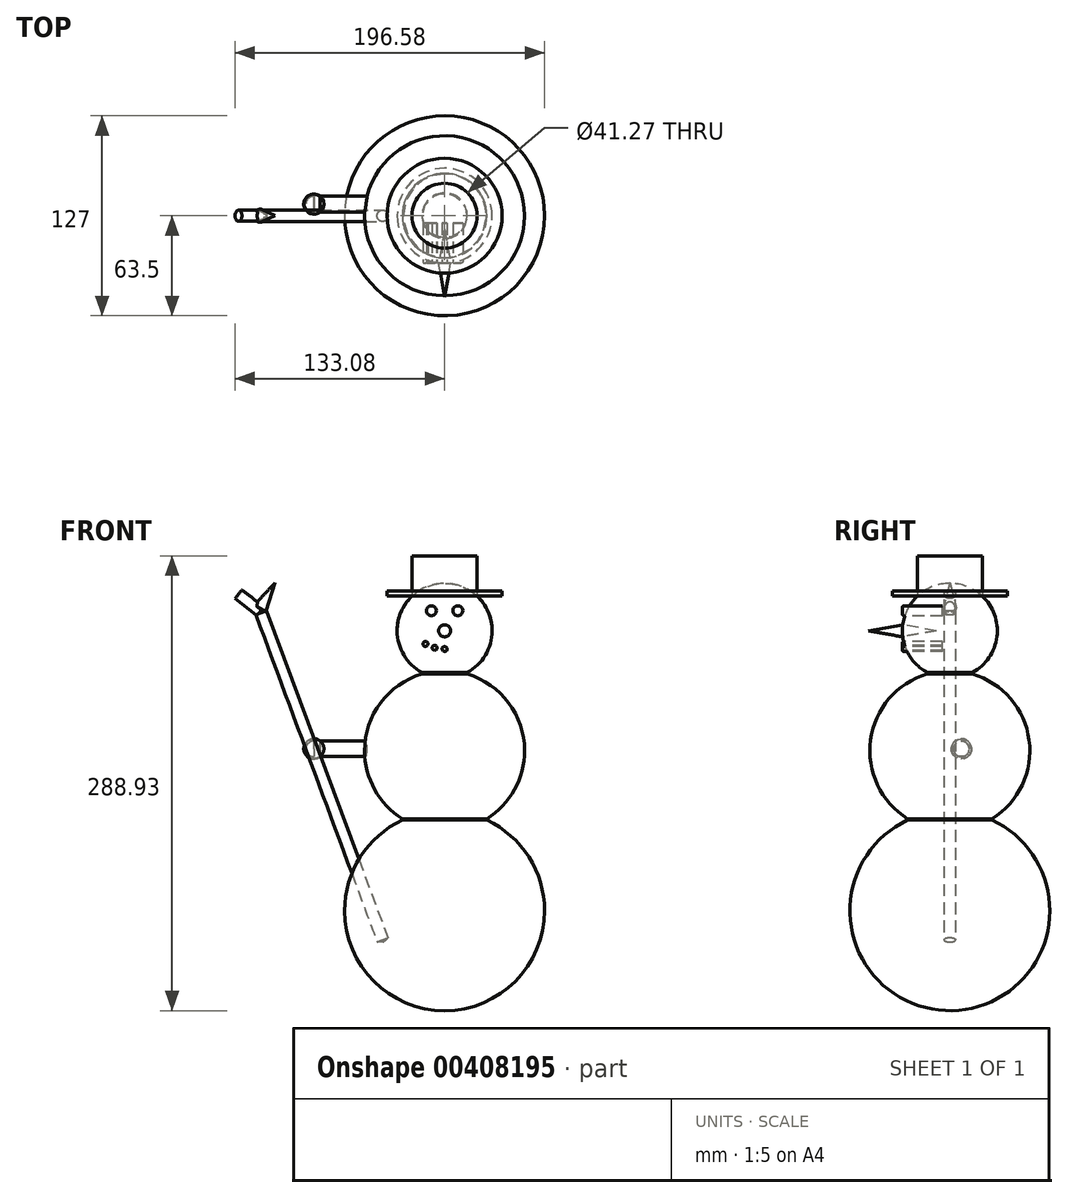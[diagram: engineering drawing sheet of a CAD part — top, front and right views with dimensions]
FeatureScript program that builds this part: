
annotation { "Feature Type Name" : "Feature", "Feature Type Description" : "" }
export const myFeature = defineFeature(function(context is Context, id is Id, definition is map)
    precondition{}
    {
        {
            var Q0;
            Q0=qCreatedBy(makeId("Top.planeOp"),FACE);
            var sketch = newSketch(context, id + "F0", { "sketchPlane" : qUnion([Q0])});
            skArc(sketch, "E0", {"start": v(63.5, 0) * mm, "mid": v(0, 63.5) * mm, "end": v(-63.5, 0) * mm});
            skLineSegment(sketch, "E1", {"start": v(-63.5, 0) * mm, "end": v(63.5, 0) * mm});
            skSolve(sketch);
        }
        {
            var Q0;
            Q0=qSketchRegion(id+"F0",true);
            var Q1;
            Q1=sQuery(id+"F0.wireOp",EDGE,"E1");
            revolve(context, id + "F1", {"entities" : qUnion([Q0]), "axis" : qUnion([Q1]), "revolveType" : RevolveType.FULL});
        }
        {
            var Q0;
            Q0=qCreatedBy(makeId("Front.planeOp"),FACE);
            var sketch = newSketch(context, id + "F2", { "sketchPlane" : qUnion([Q0])});
            skLineSegment(sketch, "E2", {"start": v(0, 0) * mm, "end": v(0, 50.8) * mm});
            skArc(sketch, "E3", {"start": v(-50.8, 101.6) * mm, "mid": v(0, 50.8) * mm, "end": v(50.8, 101.6) * mm});
            skLineSegment(sketch, "E4", {"start": v(0, 101.6) * mm, "end": v(50.8, 101.6) * mm});
            skLineSegment(sketch, "E5", {"start": v(50.8, 101.6) * mm, "end": v(0, 101.6) * mm});
            skLineSegment(sketch, "E6", {"start": v(-50.8, 101.6) * mm, "end": v(0, 101.6) * mm});
            skSolve(sketch);
        }
        {
            var Q0;
            Q0=qSketchRegion(id+"F2",true);
            var Q1;
            Q1=sQuery(id+"F2.wireOp",EDGE,"E5");
            revolve(context, id + "F3", {"operationType" : NewBodyOperationType.ADD, "entities" : qUnion([Q0]), "axis" : qUnion([Q1]), "revolveType" : RevolveType.FULL});
        }
        {
            var Q0;
            Q0=qCreatedBy(makeId("Front.planeOp"),FACE);
            var sketch = newSketch(context, id + "F4", { "sketchPlane" : qUnion([Q0])});
            skLineSegment(sketch, "E7", {"start": v(0, 177.8) * mm, "end": v(0, 0) * mm});
            skArc(sketch, "E8", {"start": v(30.16, 177.8) * mm, "mid": v(0, 207.96) * mm, "end": v(-30.16, 177.8) * mm});
            skLineSegment(sketch, "E9", {"start": v(0, 177.8) * mm, "end": v(30.16, 177.8) * mm});
            skLineSegment(sketch, "E10", {"start": v(0, 177.8) * mm, "end": v(-30.16, 177.8) * mm});
            skSolve(sketch);
        }
        {
            var Q0;
            Q0=qSketchRegion(id+"F4",true);
            var Q1;
            Q1=sQuery(id+"F4.wireOp",EDGE,"E10");
            revolve(context, id + "F5", {"operationType" : NewBodyOperationType.ADD, "entities" : qUnion([Q0]), "axis" : qUnion([Q1]), "revolveType" : RevolveType.FULL});
        }
        {
            var Q0;
            Q0=makeQuery(id+"F3.boolean.opBoolean","INTERSECT",EDGE,{"derivedFrom":[makeQuery(id+"F1.opRevolve","SWEPT_FACE",FACE,{"disambiguationData":[OSD([sQuery(id+"F0.wireOp",EDGE,"E0")])]}),makeQuery(id+"F3.opRevolve","SWEPT_FACE",FACE,{"disambiguationData":[OSD([sQuery(id+"F2.wireOp",EDGE,"E3")])]})]});
            var Q1;
            Q1=makeQuery(id+"F5.boolean.opBoolean","INTERSECT",EDGE,{"derivedFrom":[makeQuery(id+"F3.opRevolve","SWEPT_FACE",FACE,{"disambiguationData":[OSD([sQuery(id+"F2.wireOp",EDGE,"E3")])]}),makeQuery(id+"F5.opRevolve","SWEPT_FACE",FACE,{"disambiguationData":[OSD([sQuery(id+"F4.wireOp",EDGE,"E8")])]})]});
            fillet(context, id + "F6", {"entities" : qUnion([Q0, Q1]), "radius" : 0.5 * mm, "tangentPropagation" : true, "allowEdgeOverflow" : false});
        }
        {
            var Q0;
            Q0=qCreatedBy(makeId("Front.planeOp"),FACE);
            cPlane(context, id + "F7", {"entities" : qUnion([Q0]), "cplaneType" : CPlaneType.OFFSET, "offset" : 30.16 * mm, "width" : 152.4 * mm, "height" : 152.4 * mm});
        }
        {
            var Q0;
            Q0=qCreatedBy(id+"F7.planeOp",FACE);
            var sketch = newSketch(context, id + "F8", { "sketchPlane" : qUnion([Q0])});
            skLineSegment(sketch, "E11", {"start": v(0, 0) * mm, "end": v(0, 177.8) * mm});
            skCircle(sketch, "E12", {"center": v(-8.4, 190.52) * mm, "radius": 3.18 * mm});
            skCircle(sketch, "E13", {"center": v(8.4, 190.52) * mm, "radius": 3.18 * mm});
            skCircle(sketch, "E14", {"center": v(0, 177.8) * mm, "radius": 3.81 * mm});
            skCircle(sketch, "E15", {"center": v(0, 166.2) * mm, "radius": 1.59 * mm});
            skCircle(sketch, "E16.1.0", {"center": v(-6.3, 167.03) * mm, "radius": 1.59 * mm});
            skCircle(sketch, "E16.2.0", {"center": v(-12.16, 169.46) * mm, "radius": 1.59 * mm});
            skPoint(sketch, "E16.center", {"position": v(0, 190.52) * mm});
            skCircle(sketch, "E17.MirrorC", {"center": v(6.3, 167.03) * mm, "radius": 1.59 * mm});
            skCircle(sketch, "E18.MirrorC", {"center": v(12.16, 169.46) * mm, "radius": 1.59 * mm});
            skSolve(sketch);
        }
        {
            var Q0;
            Q0=makeQuery(id+"F8.imprint","IMPRINT",FACE,{"disambiguationData":[TD([[makeQuery(id+"F8.imprint","IMPRINT",EDGE,{"derivedFrom":sQuery(id+"F8.wireOp",EDGE,"E12")}),1.0]])]});
            var Q1;
            Q1=makeQuery(id+"F8.imprint","IMPRINT",FACE,{"disambiguationData":[TD([[makeQuery(id+"F8.imprint","IMPRINT",EDGE,{"derivedFrom":sQuery(id+"F8.wireOp",EDGE,"E13")}),1.0]])]});
            var Q2;
            Q2=makeQuery(id+"F8.imprint","IMPRINT",FACE,{"disambiguationData":[TD([[makeQuery(id+"F8.imprint","IMPRINT",EDGE,{"derivedFrom":sQuery(id+"F8.wireOp",EDGE,"E16.2.0")}),1.0]])]});
            var Q3;
            Q3=makeQuery(id+"F8.imprint","IMPRINT",FACE,{"disambiguationData":[TD([[makeQuery(id+"F8.imprint","IMPRINT",EDGE,{"derivedFrom":sQuery(id+"F8.wireOp",EDGE,"E16.1.0")}),1.0]])]});
            var Q4;
            {var subQ0=sQuery(id+"F8.wireOp",EDGE,"E15");var subQ1=sQuery(id+"F8.wireOp",EDGE,"E11");var subQ2=makeQuery(id+"F8.imprint","INTERSECT",VERTEX,{"disambiguationData":[OD(0.0)],"derivedFrom":[subQ1,subQ0]});Q4=makeQuery(id+"F8.imprint","IMPRINT",FACE,{"disambiguationData":[TD([[makeQuery(id+"F8.imprint","IMPRINT",EDGE,{"disambiguationData":[TD([[subQ2,-1.0]])],"derivedFrom":subQ1}),-1.0]])]});}
            var Q5;
            Q5=makeQuery(id+"F8.imprint","IMPRINT",FACE,{"disambiguationData":[TD([[makeQuery(id+"F8.imprint","IMPRINT",EDGE,{"derivedFrom":sQuery(id+"F8.wireOp",EDGE,"E17.MirrorC")}),-1.0]])]});
            var Q6;
            Q6=makeQuery(id+"F8.imprint","IMPRINT",FACE,{"disambiguationData":[TD([[makeQuery(id+"F8.imprint","IMPRINT",EDGE,{"derivedFrom":sQuery(id+"F8.wireOp",EDGE,"E18.MirrorC")}),-1.0]])]});
            var Q7;
            {var subQ0=sQuery(id+"F8.wireOp",EDGE,"E15");var subQ1=sQuery(id+"F8.wireOp",EDGE,"E11");var subQ2=makeQuery(id+"F8.imprint","INTERSECT",VERTEX,{"disambiguationData":[OD(0.0)],"derivedFrom":[subQ1,subQ0]});Q7=makeQuery(id+"F8.imprint","IMPRINT",FACE,{"disambiguationData":[TD([[makeQuery(id+"F8.imprint","IMPRINT",EDGE,{"disambiguationData":[TD([[subQ2,-1.0]])],"derivedFrom":subQ1}),1.0]])]});}
            var Q8;
            Q8=sQuery(id+"F8.wireOp",EDGE,"E12");
            var Q9;
            Q9=sQuery(id+"F8.wireOp",EDGE,"E13");
            var Q10;
            Q10=sQuery(id+"F8.wireOp",EDGE,"E18.MirrorC");
            var Q11;
            Q11=sQuery(id+"F8.wireOp",EDGE,"E17.MirrorC");
            var Q12;
            Q12=sQuery(id+"F8.wireOp",EDGE,"E15");
            var Q13;
            Q13=sQuery(id+"F8.wireOp",EDGE,"E16.1.0");
            var Q14;
            Q14=sQuery(id+"F8.wireOp",EDGE,"E16.2.0");
            extrude(context, id + "F9", {"entities" : qUnion([Q0, Q1, Q2, Q3, Q4, Q5, Q6, Q7]), "surfaceEntities" : qUnion([Q8, Q9, Q10, Q11, Q12, Q13, Q14]), "oppositeDirection" : true, "depth" : 25.4 * mm});
        }
        {
            var Q0;
            Q0=makeQuery(id+"F9.opExtrude","CAP_EDGE",EDGE,{"disambiguationData":[OSD([sQuery(id+"F8.wireOp",EDGE,"E12")])],"isStart":true});
            var Q1;
            Q1=makeQuery(id+"F9.opExtrude","CAP_EDGE",EDGE,{"disambiguationData":[OSD([sQuery(id+"F8.wireOp",EDGE,"E13")])],"isStart":true});
            var Q2;
            Q2=makeQuery(id+"F9.opExtrude","CAP_EDGE",EDGE,{"disambiguationData":[OSD([sQuery(id+"F8.wireOp",EDGE,"E16.2.0")])],"isStart":true});
            var Q3;
            Q3=makeQuery(id+"F9.opExtrude","CAP_EDGE",EDGE,{"disambiguationData":[OSD([sQuery(id+"F8.wireOp",EDGE,"E16.1.0")])],"isStart":true});
            var Q4;
            Q4=makeQuery(id+"F9.opExtrude","CAP_EDGE",EDGE,{"disambiguationData":[OSD([sQuery(id+"F8.wireOp",EDGE,"E15")])],"isStart":true});
            var Q5;
            Q5=makeQuery(id+"F9.opExtrude","CAP_EDGE",EDGE,{"disambiguationData":[OSD([sQuery(id+"F8.wireOp",EDGE,"E17.MirrorC")])],"isStart":true});
            var Q6;
            Q6=makeQuery(id+"F9.opExtrude","CAP_EDGE",EDGE,{"disambiguationData":[OSD([sQuery(id+"F8.wireOp",EDGE,"E18.MirrorC")])],"isStart":true});
            fillet(context, id + "F10", {"entities" : qUnion([Q0, Q1, Q2, Q3, Q4, Q5, Q6]), "radius" : 1.27 * mm, "tangentPropagation" : true, "rho" : 0.5, "crossSection" : FilletCrossSection.CONIC, "allowEdgeOverflow" : false});
        }
        {
            var Q0;
            Q0=makeQuery(id+"F8.imprint","IMPRINT",FACE,{"disambiguationData":[TD([[makeQuery(id+"F8.imprint","IMPRINT",EDGE,{"derivedFrom":sQuery(id+"F8.wireOp",EDGE,"E14")}),1.0]])]});
            extrude(context, id + "F11", {"entities" : qUnion([Q0]), "endBound" : BoundingType.SYMMETRIC, "depth" : 50.8 * mm, "hasDraft" : true, "draftAngle" : 10 * degree, "draftPullDirection" : true});
        }
        {
            var Q0;
            Q0=qCreatedBy(makeId("Top.planeOp"),FACE);
            cPlane(context, id + "F12", {"entities" : qUnion([Q0]), "cplaneType" : CPlaneType.OFFSET, "offset" : 200.02 * mm, "width" : 152.4 * mm, "height" : 152.4 * mm});
        }
        {
            var Q0;
            Q0=qCreatedBy(id+"F12.planeOp",FACE);
            var sketch = newSketch(context, id + "F13", { "sketchPlane" : qUnion([Q0])});
            skCircle(sketch, "E19", {"center": v(0, 0) * mm, "radius": 36.51 * mm});
            skCircle(sketch, "E20", {"center": v(0, 0) * mm, "radius": 20.64 * mm});
            skSolve(sketch);
        }
        {
            var Q0;
            Q0=qSketchRegion(id+"F13",true);
            extrude(context, id + "F14", {"entities" : qUnion([Q0]), "depth" : 3.17 * mm});
        }
        {
            var Q0;
            Q0=makeQuery(id+"F13.imprint","IMPRINT",FACE,{"disambiguationData":[TD([[makeQuery(id+"F13.imprint","IMPRINT",EDGE,{"derivedFrom":sQuery(id+"F13.wireOp",EDGE,"E20")}),1.0]])]});
            extrude(context, id + "F15", {"entities" : qUnion([Q0]), "depth" : 25.4 * mm});
        }
        {
            var Q0;
            Q0=qCreatedBy(makeId("Right.planeOp"),FACE);
            var sketch = newSketch(context, id + "F16", { "sketchPlane" : qUnion([Q0])});
            skCircle(sketch, "E21", {"center": v(7.36, 102.84) * mm, "radius": 5 * mm});
            skSolve(sketch);
        }
        {
            var Q0;
            Q0 = qSketchRegion(id + "F16", true);
            extrude(context, id + "F17", {"entities" : qUnion([Q0]), "operationType" : NewBodyOperationType.ADD, "oppositeDirection" : true, "depth" : 83.06 * mm});
        }
        {
            var Q0;
            Q0=makeQuery(id+"F17.opExtrude","CAP_FACE",FACE,{"disambiguationData":[OSD([sQuery(id+"F16.wireOp",EDGE,"E21")])],"isStart":false});
            var sketch = newSketch(context, id + "F18", { "sketchPlane" : qUnion([Q0])});
            skLineSegment(sketch, "E22", {"start": v(-7.36, 102.84) * mm, "end": v(-13.7, 102.84) * mm});
            skLineSegment(sketch, "E23", {"start": v(-13.7, 102.84) * mm, "end": v(-7.36, 102.84) * mm});
            skLineSegment(sketch, "E24", {"start": v(-1, 102.84) * mm, "end": v(-7.36, 102.84) * mm});
            skArc(sketch, "E25", {"start": v(-1, 102.84) * mm, "mid": v(-7.36, 109.14) * mm, "end": v(-13.7, 102.84) * mm});
            skSolve(sketch);
        }
        {
            var Q0;
            {var subQ0=sQuery(id+"F18.wireOp",EDGE,"E25");Q0=makeQuery(id+"F18.imprint","IMPRINT",FACE,{"disambiguationData":[TD([[makeQuery(id+"F18.imprint","IMPRINT",EDGE,{"derivedFrom":subQ0}),1.0]])]});}
            var Q1;
            {var subQ0=sQuery(id+"F18.wireOp",EDGE,"E24");var subQ1=sQuery(id+"F18.wireOp",EDGE,"E23");var subQ2=makeQuery(id+"F18.imprint","INTERSECT",VERTEX,{"derivedFrom":[subQ1,subQ0]});Q1=makeQuery(id+"F18.imprint","IMPRINT",FACE,{"disambiguationData":[TD([[makeQuery(id+"F18.imprint","IMPRINT",EDGE,{"disambiguationData":[TD([[subQ2,1.0]])],"derivedFrom":subQ1}),1.0]])]});}
            var Q2;
            Q2=sQuery(id+"F18.wireOp",EDGE,"E24");
            revolve(context, id + "F19", {"operationType" : NewBodyOperationType.ADD, "entities" : qUnion([Q0, Q1]), "axis" : qUnion([Q2]), "revolveType" : RevolveType.FULL});
        }
        {
            var Q0;
            Q0=qCreatedBy(makeId("Front.planeOp"),FACE);
            var sketch = newSketch(context, id + "F20", { "sketchPlane" : qUnion([Q0])});
            skLineSegment(sketch, "E26", {"start": v(-38.93, -19.85) * mm, "end": v(-116.36, 189.26) * mm});
            skLineSegment(sketch, "E27", {"start": v(-116.36, 189.26) * mm, "end": v(-119.81, 187.98) * mm});
            skLineSegment(sketch, "E28", {"start": v(-119.81, 187.98) * mm, "end": v(-42.85, -19.85) * mm});
            skLineSegment(sketch, "E29", {"start": v(-42.85, -19.85) * mm, "end": v(-38.93, -19.85) * mm});
            skSolve(sketch);
        }
        {
            var Q0;
            Q0=makeQuery(id+"F20.imprint","IMPRINT",FACE,{"disambiguationData":[TD([[makeQuery(id+"F20.imprint","IMPRINT",EDGE,{"derivedFrom":sQuery(id+"F20.wireOp",EDGE,"E26")}),1.0]])]});
            var Q1;
            Q1=sQuery(id+"F20.wireOp",EDGE,"E26");
            revolve(context, id + "F21", {"entities" : qUnion([Q0]), "axis" : qUnion([Q1]), "revolveType" : RevolveType.FULL});
        }
        {
            var Q0;
            Q0=qCreatedBy(makeId("Front.planeOp"),FACE);
            var sketch = newSketch(context, id + "F22", { "sketchPlane" : qUnion([Q0])});
            skLineSegment(sketch, "E30", {"start": v(-119.24, 187.39) * mm, "end": v(-133.08, 198.23) * mm});
            skLineSegment(sketch, "E31", {"start": v(-133.08, 198.23) * mm, "end": v(-130.9, 201.03) * mm});
            skLineSegment(sketch, "E32", {"start": v(-130.9, 201.03) * mm, "end": v(-113.49, 187.39) * mm});
            skLineSegment(sketch, "E33", {"start": v(-113.49, 187.39) * mm, "end": v(-119.24, 187.39) * mm});
            skSolve(sketch);
        }
        {
            var Q0;
            Q0=makeQuery(id+"F22.imprint","IMPRINT",FACE,{"disambiguationData":[TD([[makeQuery(id+"F22.imprint","IMPRINT",EDGE,{"derivedFrom":sQuery(id+"F22.wireOp",EDGE,"E30")}),-1.0]])]});
            var Q1;
            Q1=sQuery(id+"F22.wireOp",EDGE,"E32");
            revolve(context, id + "F23", {"operationType" : NewBodyOperationType.ADD, "entities" : qUnion([Q0]), "axis" : qUnion([Q1]), "revolveType" : RevolveType.FULL});
        }
        {
            var Q0;
            Q0=qCreatedBy(makeId("Front.planeOp"),FACE);
            var sketch = newSketch(context, id + "F24", { "sketchPlane" : qUnion([Q0])});
            skLineSegment(sketch, "E34", {"start": v(-113.53, 190) * mm, "end": v(-107.55, 208.33) * mm});
            skLineSegment(sketch, "E35", {"start": v(-107.55, 208.33) * mm, "end": v(-118.4, 190) * mm});
            skLineSegment(sketch, "E36", {"start": v(-118.4, 190) * mm, "end": v(-113.53, 190) * mm});
            skSolve(sketch);
        }
        {
            var Q0;
            Q0=makeQuery(id+"F24.imprint","IMPRINT",FACE,{"disambiguationData":[TD([[makeQuery(id+"F24.imprint","IMPRINT",EDGE,{"derivedFrom":sQuery(id+"F24.wireOp",EDGE,"E34")}),1.0]])]});
            var Q1;
            Q1=sQuery(id+"F24.wireOp",EDGE,"E35");
            revolve(context, id + "F25", {"operationType" : NewBodyOperationType.ADD, "entities" : qUnion([Q0]), "axis" : qUnion([Q1]), "revolveType" : RevolveType.FULL});
        }
    });
